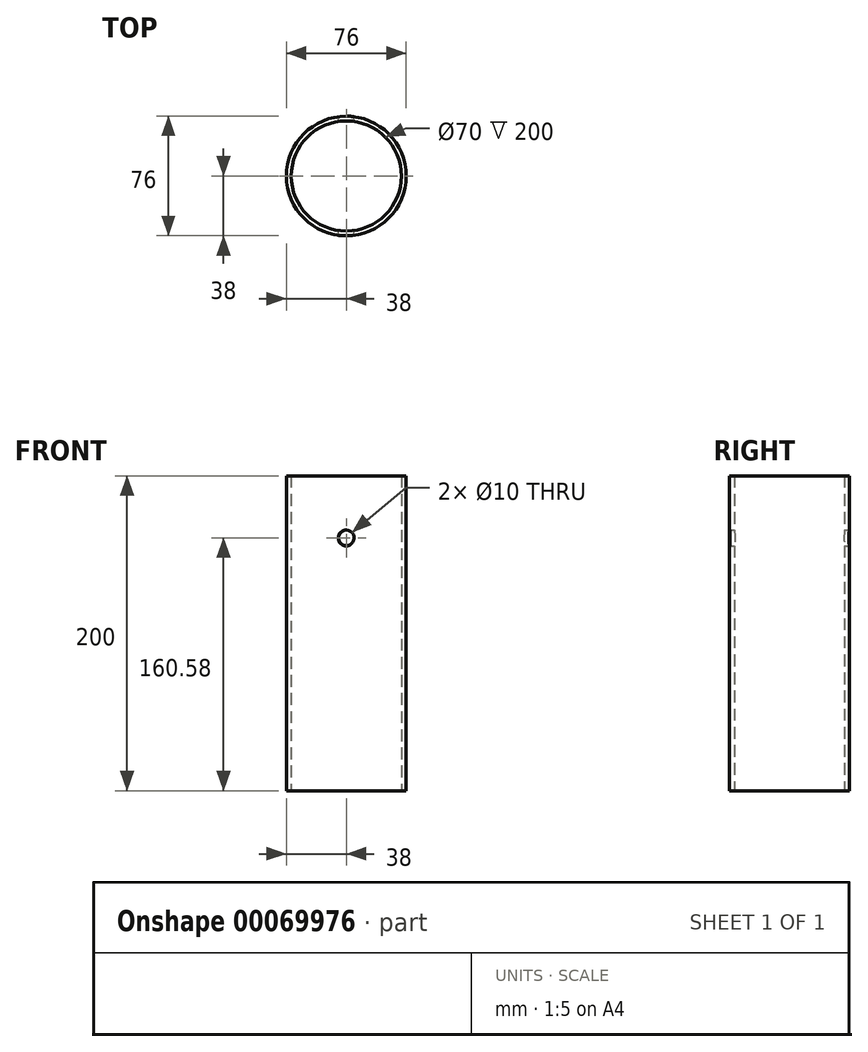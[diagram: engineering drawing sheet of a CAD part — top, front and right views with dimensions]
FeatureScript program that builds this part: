
annotation { "Feature Type Name" : "Feature", "Feature Type Description" : "" }
export const myFeature = defineFeature(function(context is Context, id is Id, definition is map)
    precondition{}
    {
        {
            var Q0;
            Q0=qCreatedBy(makeId("Top.planeOp"),FACE);
            var sketch = newSketch(context, id + "F0", { "sketchPlane" : qUnion([Q0])});
            skCircle(sketch, "E0", {"center": v(0, 0) * mm, "radius": 35 * mm});
            skCircle(sketch, "E1.0", {"center": v(0, 0) * mm, "radius": 38 * mm});
            skSolve(sketch);
        }
        {
            var Q0;
            Q0=makeQuery(id+"F0.imprint","IMPRINT",FACE,{"disambiguationData":[TD([[makeQuery(id+"F0.imprint","IMPRINT",EDGE,{"derivedFrom":sQuery(id+"F0.wireOp",EDGE,"E0")}),-1.0]])]});
            extrude(context, id + "F1", {"entities" : qUnion([Q0]), "depth" : 200 * mm});
        }
        {
            var Q0;
            Q0=qCreatedBy(makeId("Front.planeOp"),FACE);
            var sketch = newSketch(context, id + "F2", { "sketchPlane" : qUnion([Q0])});
            skCircle(sketch, "E2", {"center": v(-62.21, -16.73) * mm, "radius": 5 * mm});
            skSolve(sketch);
        }
        {
            var Q0;
            Q0=makeQuery(id+"F2.imprint","IMPRINT",FACE,{"disambiguationData":[TD([[makeQuery(id+"F2.imprint","IMPRINT",EDGE,{"derivedFrom":sQuery(id+"F2.wireOp",EDGE,"E2")}),1.0]])]});
            extrude(context, id + "F3", {"entities" : qUnion([Q0]), "depth" : 125 * mm});
        }
        {
            var Q0;
            Q0=makeQuery(id+"F3.opExtrude","SWEPT_BODY",BODY,{"disambiguationData":[OSD([sQuery(id+"F2.wireOp",EDGE,"E2")])]});
            transform(context, id + "F4", {"entities" : qUnion([Q0]), "transformType" : TransformType.TRANSLATION_3D, "dx" : 62.2 * mm, "dy" : 60.45 * mm, "dz" : 177.3 * mm, "makeCopy" : false});
        }
        {
            var Q0;
            Q0=makeQuery(id+"F3.opExtrude","SWEPT_BODY",BODY,{"disambiguationData":[OSD([sQuery(id+"F2.wireOp",EDGE,"E2")])]});
            var Q1;
            Q1=makeQuery(id+"F1.opExtrude","SWEPT_BODY",BODY,{"disambiguationData":[OSD([sQuery(id+"F0.wireOp",EDGE,"E0"),sQuery(id+"F0.wireOp",EDGE,"E1.0")])]});
            booleanBodies(context, id + "F5", {"operationType" : BooleanOperationType.SUBTRACTION, "tools" : qUnion([Q0]), "targets" : qUnion([Q1])});
        }
    });
